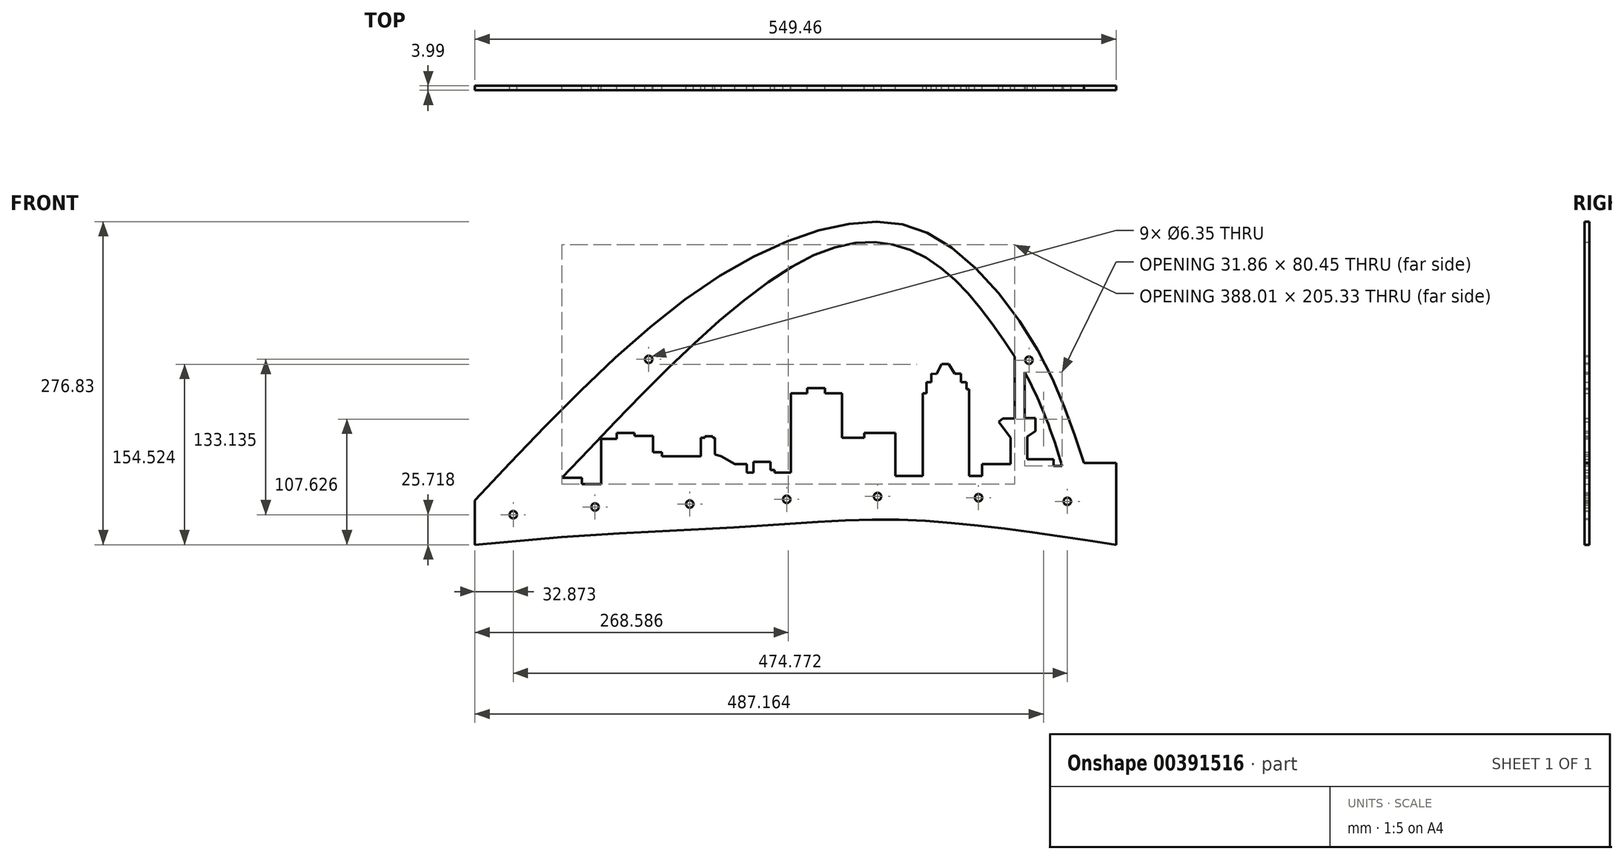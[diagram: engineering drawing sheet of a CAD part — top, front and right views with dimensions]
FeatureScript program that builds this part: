
annotation { "Feature Type Name" : "Feature", "Feature Type Description" : "" }
export const myFeature = defineFeature(function(context is Context, id is Id, definition is map)
    precondition{}
    {
        {
            var Q0;
            Q0=qCreatedBy(makeId("Front.planeOp"),FACE);
            var sketch = newSketch(context, id + "F0", { "sketchPlane" : qUnion([Q0])});
            skLineSegment(sketch, "E0", {"start": v(-89.7, -121.98) * mm, "end": v(-72.63, -121.98) * mm});
            skLineSegment(sketch, "E1", {"start": v(-72.63, -121.98) * mm, "end": v(-72.63, -127.47) * mm});
            skLineSegment(sketch, "E2", {"start": v(-72.63, -127.47) * mm, "end": v(-56.16, -127.47) * mm});
            skLineSegment(sketch, "E3", {"start": v(-56.16, -127.47) * mm, "end": v(-56.16, -88.5) * mm});
            skLineSegment(sketch, "E4", {"start": v(-56.16, -88.5) * mm, "end": v(-42.62, -88.5) * mm});
            skLineSegment(sketch, "E5", {"start": v(-42.62, -88.5) * mm, "end": v(-42.62, -83.62) * mm});
            skLineSegment(sketch, "E6", {"start": v(-42.62, -83.62) * mm, "end": v(-27.52, -83.62) * mm});
            skLineSegment(sketch, "E7", {"start": v(-27.52, -83.62) * mm, "end": v(-27.52, -86.21) * mm});
            skLineSegment(sketch, "E8", {"start": v(-27.52, -86.21) * mm, "end": v(-11.8, -86.21) * mm});
            skLineSegment(sketch, "E9", {"start": v(-11.8, -86.21) * mm, "end": v(-11.8, -100.01) * mm});
            skLineSegment(sketch, "E10", {"start": v(-11.8, -100.01) * mm, "end": v(-4.12, -100.01) * mm});
            skLineSegment(sketch, "E11", {"start": v(-4.12, -100.01) * mm, "end": v(-4.12, -103.6) * mm});
            skLineSegment(sketch, "E12", {"start": v(-4.12, -103.6) * mm, "end": v(25.63, -103.6) * mm});
            skLineSegment(sketch, "E13", {"start": v(25.63, -103.6) * mm, "end": v(29.4, -103.6) * mm});
            skLineSegment(sketch, "E14", {"start": v(29.4, -103.6) * mm, "end": v(29.4, -87.67) * mm});
            skLineSegment(sketch, "E15", {"start": v(29.4, -87.67) * mm, "end": v(32.7, -87.67) * mm});
            skLineSegment(sketch, "E16", {"start": v(32.7, -87.67) * mm, "end": v(32.7, -86.42) * mm});
            skLineSegment(sketch, "E17", {"start": v(32.7, -86.42) * mm, "end": v(39.32, -86.42) * mm});
            skLineSegment(sketch, "E18", {"start": v(39.32, -86.42) * mm, "end": v(39.32, -87.67) * mm});
            skLineSegment(sketch, "E19", {"start": v(39.32, -87.67) * mm, "end": v(41.24, -87.67) * mm});
            skLineSegment(sketch, "E20", {"start": v(41.24, -87.67) * mm, "end": v(41.24, -102.06) * mm});
            skLineSegment(sketch, "E21", {"start": v(41.24, -102.06) * mm, "end": v(46.72, -103.6) * mm});
            skLineSegment(sketch, "E22", {"start": v(46.72, -103.6) * mm, "end": v(58.37, -110.3) * mm});
            skLineSegment(sketch, "E23", {"start": v(58.37, -110.3) * mm, "end": v(68.72, -110.3) * mm});
            skLineSegment(sketch, "E24", {"start": v(68.72, -110.3) * mm, "end": v(68.72, -117.64) * mm});
            skLineSegment(sketch, "E25", {"start": v(68.72, -117.64) * mm, "end": v(74.33, -117.64) * mm});
            skLineSegment(sketch, "E26", {"start": v(74.33, -117.64) * mm, "end": v(74.33, -108.35) * mm});
            skLineSegment(sketch, "E27", {"start": v(74.33, -108.35) * mm, "end": v(88.95, -108.35) * mm});
            skLineSegment(sketch, "E28", {"start": v(88.95, -108.35) * mm, "end": v(88.95, -115.24) * mm});
            skLineSegment(sketch, "E29", {"start": v(88.95, -115.24) * mm, "end": v(92.58, -115.24) * mm});
            skLineSegment(sketch, "E30", {"start": v(92.58, -115.24) * mm, "end": v(92.58, -117.64) * mm});
            skLineSegment(sketch, "E31", {"start": v(92.58, -117.64) * mm, "end": v(106.46, -117.64) * mm});
            skLineSegment(sketch, "E32", {"start": v(106.46, -117.64) * mm, "end": v(106.46, -49.48) * mm});
            skLineSegment(sketch, "E33", {"start": v(106.46, -49.48) * mm, "end": v(120.26, -49.48) * mm});
            skLineSegment(sketch, "E34", {"start": v(120.26, -49.48) * mm, "end": v(120.26, -45.07) * mm});
            skLineSegment(sketch, "E35", {"start": v(120.26, -45.07) * mm, "end": v(135.58, -45.07) * mm});
            skLineSegment(sketch, "E36", {"start": v(135.58, -45.07) * mm, "end": v(135.58, -49.48) * mm});
            skLineSegment(sketch, "E37", {"start": v(135.58, -49.48) * mm, "end": v(150.34, -49.48) * mm});
            skLineSegment(sketch, "E38", {"start": v(150.34, -49.48) * mm, "end": v(150.34, -87.67) * mm});
            skLineSegment(sketch, "E39", {"start": v(150.34, -87.67) * mm, "end": v(169.31, -87.67) * mm});
            skLineSegment(sketch, "E40", {"start": v(169.31, -87.67) * mm, "end": v(169.31, -83.62) * mm});
            skLineSegment(sketch, "E41", {"start": v(169.31, -83.62) * mm, "end": v(195.84, -83.62) * mm});
            skLineSegment(sketch, "E42", {"start": v(195.84, -83.62) * mm, "end": v(195.84, -120.22) * mm});
            skLineSegment(sketch, "E43", {"start": v(195.84, -120.22) * mm, "end": v(219.53, -120.22) * mm});
            skLineSegment(sketch, "E44", {"start": v(219.53, -120.22) * mm, "end": v(219.53, -49.48) * mm});
            skLineSegment(sketch, "E45", {"start": v(219.53, -49.48) * mm, "end": v(222.58, -49.48) * mm});
            skLineSegment(sketch, "E46", {"start": v(222.58, -49.48) * mm, "end": v(222.58, -44.92) * mm});
            skLineSegment(sketch, "E47", {"start": v(222.58, -40.04) * mm, "end": v(226.85, -40.04) * mm});
            skLineSegment(sketch, "E48", {"start": v(226.85, -40.04) * mm, "end": v(226.85, -32.85) * mm});
            skLineSegment(sketch, "E49", {"start": v(235.7, -24.42) * mm, "end": v(241.68, -24.42) * mm});
            skLineSegment(sketch, "E50", {"start": v(241.68, -24.42) * mm, "end": v(246.75, -32.85) * mm});
            skLineSegment(sketch, "E51", {"start": v(246.75, -32.85) * mm, "end": v(252.25, -32.85) * mm});
            skLineSegment(sketch, "E52", {"start": v(252.25, -32.85) * mm, "end": v(252.25, -40.04) * mm});
            skLineSegment(sketch, "E53", {"start": v(252.25, -40.04) * mm, "end": v(256.82, -40.04) * mm});
            skLineSegment(sketch, "E54", {"start": v(256.82, -40.04) * mm, "end": v(256.82, -46.24) * mm});
            skLineSegment(sketch, "E55", {"start": v(256.82, -46.24) * mm, "end": v(259.1, -46.24) * mm});
            skLineSegment(sketch, "E56", {"start": v(259.1, -46.24) * mm, "end": v(259.1, -120.22) * mm});
            skLineSegment(sketch, "E57", {"start": v(259.1, -120.22) * mm, "end": v(270.43, -120.22) * mm});
            skLineSegment(sketch, "E58", {"start": v(270.43, -120.22) * mm, "end": v(270.43, -110.3) * mm});
            skLineSegment(sketch, "E59", {"start": v(270.43, -110.3) * mm, "end": v(294.87, -110.3) * mm});
            skLineSegment(sketch, "E60", {"start": v(294.87, -110.3) * mm, "end": v(294.87, -87.67) * mm});
            skLineSegment(sketch, "E61", {"start": v(294.87, -87.67) * mm, "end": v(284.45, -73.95) * mm});
            skLineSegment(sketch, "E62", {"start": v(284.45, -73.95) * mm, "end": v(287.97, -71.27) * mm});
            skLineSegment(sketch, "E63", {"start": v(222.58, -40.04) * mm, "end": v(222.58, -44.92) * mm});
            skLineSegment(sketch, "E64", {"start": v(287.97, -71.27) * mm, "end": v(298.3, -71.27) * mm});
            skLineSegment(sketch, "E65", {"start": v(298.3, -71.27) * mm, "end": v(298.3, -18.05) * mm});
            skFitSpline(sketch, "E66", {"points": [v(-89.7, -121.98) * mm, v(140.18, 74.29) * mm, v(231.6, 60.48) * mm, v(298.3, -18.05) * mm], "startDerivative": vector(528.74, 559.34) * mm, "endDerivative": vector(221.4, -327.68) * mm});
            skLineSegment(sketch, "E67", {"start": v(306.94, -31.48) * mm, "end": v(306.94, -70.84) * mm});
            skLineSegment(sketch, "E68", {"start": v(306.94, -70.84) * mm, "end": v(316, -70.84) * mm});
            skLineSegment(sketch, "E69", {"start": v(316, -70.84) * mm, "end": v(316, -82.06) * mm});
            skLineSegment(sketch, "E70", {"start": v(316, -82.06) * mm, "end": v(309.1, -86.8) * mm});
            skLineSegment(sketch, "E71", {"start": v(309.1, -86.8) * mm, "end": v(309.1, -106.12) * mm});
            skLineSegment(sketch, "E72", {"start": v(309.1, -106.12) * mm, "end": v(331.55, -106.12) * mm});
            skLineSegment(sketch, "E73", {"start": v(331.55, -106.12) * mm, "end": v(331.55, -111.93) * mm});
            skLineSegment(sketch, "E74", {"start": v(331.55, -111.93) * mm, "end": v(338.8, -111.93) * mm});
            skArc(sketch, "E75", {"start": v(338.8, -111.93) * mm, "mid": v(325, -70.86) * mm, "end": v(306.94, -31.48) * mm});
            skFitSpline(sketch, "E76", {"points": [v(-164.29, -141.35) * mm, v(27.2, 39.02) * mm, v(158.32, 95.98) * mm, v(235.09, 81.31) * mm, v(317.03, -11.03) * mm, v(357.57, -109.42) * mm], "startDerivative": vector(693.22, 737.48) * mm, "endDerivative": vector(180.95, -551.52) * mm});
            skLineSegment(sketch, "E77", {"start": v(357.57, -109.42) * mm, "end": v(385.17, -109.42) * mm});
            skLineSegment(sketch, "E78", {"start": v(385.17, -109.42) * mm, "end": v(385.17, -139.63) * mm});
            skLineSegment(sketch, "E79", {"start": v(385.17, -139.63) * mm, "end": v(385.17, -179.33) * mm});
            skFitSpline(sketch, "E80", {"points": [v(385.17, -179.33) * mm, v(275.63, -163.8) * mm, v(177.3, -157.75) * mm, v(69.47, -163.8) * mm, v(-46.11, -169.83) * mm, v(-164.29, -179.33) * mm], "startDerivative": vector(-555.33, 85.44) * mm, "endDerivative": vector(-570.36, -51.26) * mm});
            skLineSegment(sketch, "E81", {"start": v(-164.29, -141.35) * mm, "end": v(-164.29, -179.33) * mm});
            skLineSegment(sketch, "E82", {"start": v(235.7, -24.42) * mm, "end": v(231.33, -33.14) * mm});
            skLineSegment(sketch, "E83", {"start": v(226.85, -32.85) * mm, "end": v(231.33, -33.14) * mm});
            skCircle(sketch, "E84", {"center": v(-131.42, -153.61) * mm, "radius": 3.18 * mm});
            skCircle(sketch, "E85", {"center": v(-61.39, -146.98) * mm, "radius": 3.18 * mm});
            skCircle(sketch, "E86", {"center": v(19.81, -144.46) * mm, "radius": 3.18 * mm});
            skCircle(sketch, "E87", {"center": v(102.9, -140.44) * mm, "radius": 3.18 * mm});
            skCircle(sketch, "E88", {"center": v(180.73, -137.98) * mm, "radius": 3.18 * mm});
            skCircle(sketch, "E89", {"center": v(267.25, -139.03) * mm, "radius": 3.18 * mm});
            skCircle(sketch, "E90", {"center": v(343.36, -142.15) * mm, "radius": 3.18 * mm});
            skCircle(sketch, "E91", {"center": v(-15.37, -20.48) * mm, "radius": 3.18 * mm});
            skCircle(sketch, "E92", {"center": v(310.48, -21.24) * mm, "radius": 3.18 * mm});
            skSolve(sketch);
        }
        {
            var Q0;
            Q0=makeQuery(id+"F0.imprint","IMPRINT",FACE,{"disambiguationData":[TD([[makeQuery(id+"F0.imprint","IMPRINT",EDGE,{"derivedFrom":sQuery(id+"F0.wireOp",EDGE,"E0")}),-1.0]])]});
            extrude(context, id + "F1", {"entities" : qUnion([Q0]), "depth" : 4 * mm});
        }
    });
